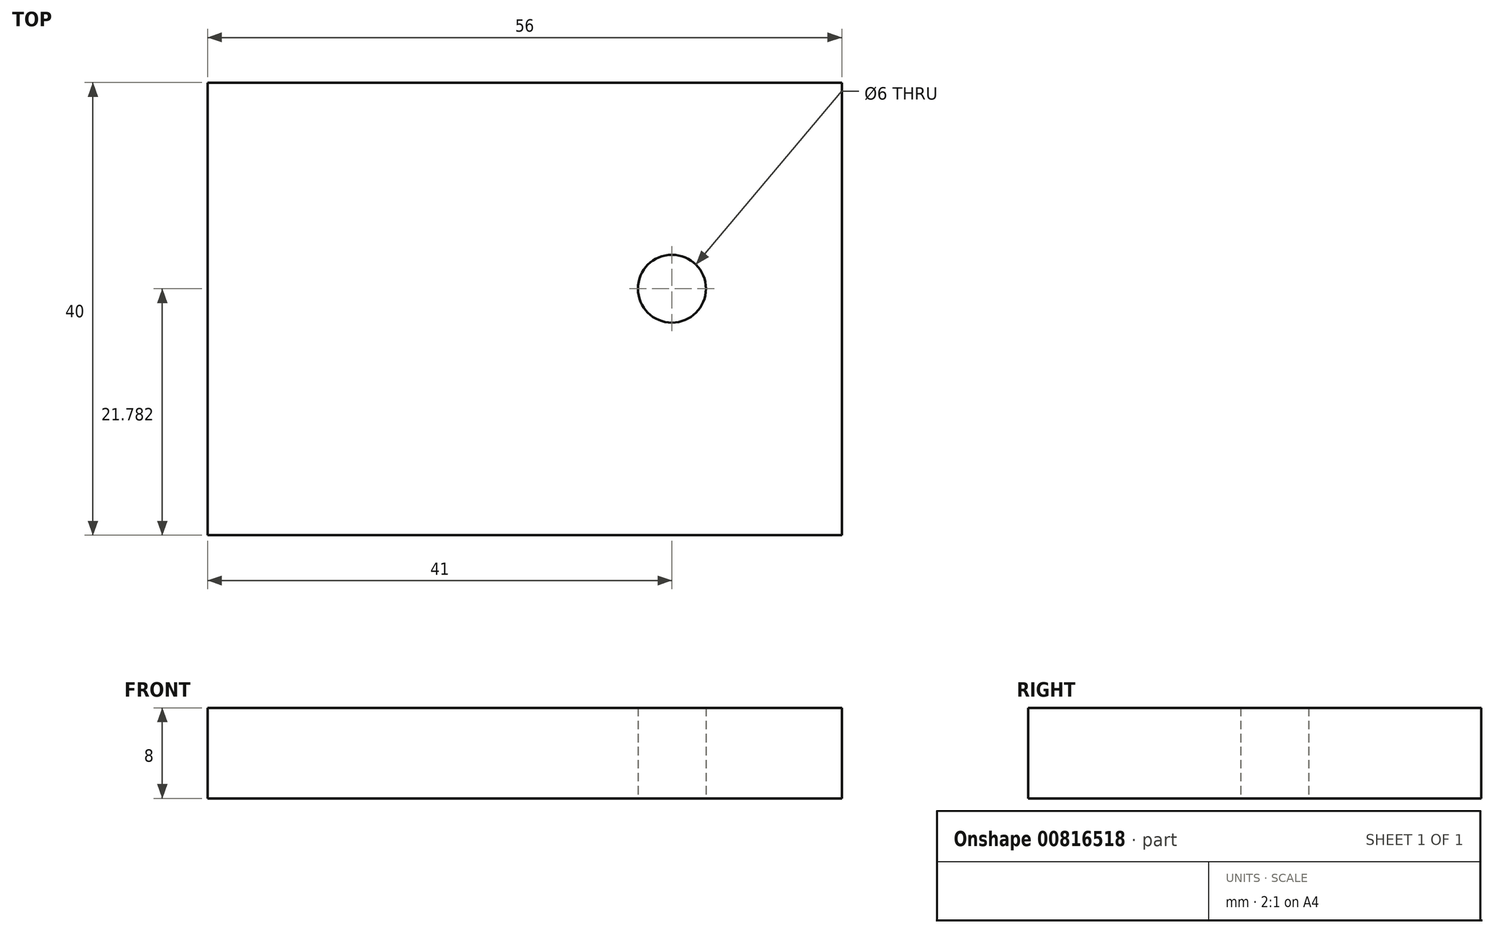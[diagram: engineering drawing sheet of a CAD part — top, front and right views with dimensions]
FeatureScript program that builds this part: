
annotation { "Feature Type Name" : "Feature", "Feature Type Description" : "" }
export const myFeature = defineFeature(function(context is Context, id is Id, definition is map)
    precondition{}
    {
        {
            var Q0;
            Q0=qCreatedBy(makeId("Right.planeOp"),FACE);
            var sketch = newSketch(context, id + "F0", { "sketchPlane" : qUnion([Q0])});
            skLineSegment(sketch, "E0.bottom", {"start": v(1.37, 0) * mm, "end": v(41.37, 0) * mm});
            skLineSegment(sketch, "E0.top", {"start": v(1.37, 8) * mm, "end": v(41.37, 8) * mm});
            skLineSegment(sketch, "E0.left", {"start": v(1.37, 0) * mm, "end": v(1.37, 8) * mm});
            skLineSegment(sketch, "E0.right", {"start": v(41.37, 0) * mm, "end": v(41.37, 8) * mm});
            skSolve(sketch);
        }
        {
            var Q0;
            Q0 = qSketchRegion(id + "F0", true);
            extrude(context, id + "F1", {"entities" : qUnion([Q0]), "depth" : 56 * mm, "offsetDistance" : 25 * mm});
        }
        {
            var Q0;
            Q0=makeQuery(id+"F1.opExtrude","SWEPT_FACE",FACE,{"disambiguationData":[OSD([sQuery(id+"F0.wireOp",EDGE,"E0.bottom")])]});
            var sketch = newSketch(context, id + "F2", { "sketchPlane" : qUnion([Q0])});
            skCircle(sketch, "E1", {"center": v(41, -23.15) * mm, "radius": 3 * mm});
            skSolve(sketch);
        }
        {
            var Q0;
            Q0=makeQuery(id+"F2.imprint","IMPRINT",FACE,{"disambiguationData":[TD([[makeQuery(id+"F2.imprint","IMPRINT",EDGE,{"derivedFrom":sQuery(id+"F2.wireOp",EDGE,"E1")}),1.0]])]});
            extrude(context, id + "F3", {"entities" : qUnion([Q0]), "operationType" : NewBodyOperationType.REMOVE, "oppositeDirection" : true, "depth" : 11.1 * mm, "offsetDistance" : 25 * mm});
        }
    });
